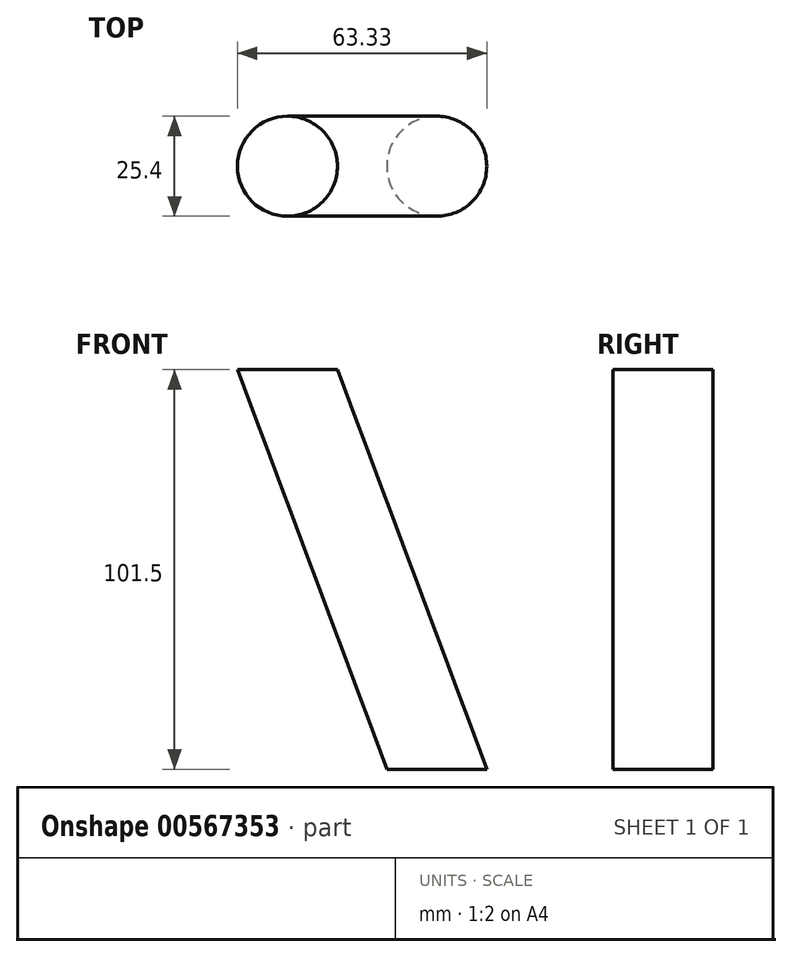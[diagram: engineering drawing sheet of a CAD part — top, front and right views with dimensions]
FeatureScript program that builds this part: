
annotation { "Feature Type Name" : "Feature", "Feature Type Description" : "" }
export const myFeature = defineFeature(function(context is Context, id is Id, definition is map)
    precondition{}
    {
        {
            var Q0;
            Q0=qCreatedBy(makeId("Front.planeOp"),FACE);
            var sketch = newSketch(context, id + "F0", { "sketchPlane" : qUnion([Q0])});
            skLineSegment(sketch, "E0", {"start": v(0, 0) * mm, "end": v(0, 74.43) * mm, "construction": true});
            skLineSegment(sketch, "E1", {"start": v(0, 0) * mm, "end": v(204.24, 0) * mm, "construction": true});
            skLineSegment(sketch, "E2.0", {"start": v(38.1, 0) * mm, "end": v(38.1, 74.43) * mm});
            skLineSegment(sketch, "E3.0", {"start": v(76.2, 0) * mm, "end": v(76.2, 74.43) * mm});
            skSolve(sketch);
        }
        {
            var Q0;
            Q0=qCreatedBy(makeId("Front.planeOp"),FACE);
            var sketch = newSketch(context, id + "F1", { "sketchPlane" : qUnion([Q0])});
            skLineSegment(sketch, "E4", {"start": v(75.9, 0) * mm, "end": v(37.98, 101.5) * mm});
            skSolve(sketch);
        }
        {
            var Q0;
            Q0=qCreatedBy(makeId("Top.planeOp"),FACE);
            var sketch = newSketch(context, id + "F2", { "sketchPlane" : qUnion([Q0])});
            skCircle(sketch, "E5", {"center": v(38.27, 0) * mm, "radius": 12.7 * mm});
            skSolve(sketch);
        }
        {
            var Q0;
            Q0=makeQuery(id+"F2.imprint","IMPRINT",FACE,{"disambiguationData":[TD([[makeQuery(id+"F2.imprint","IMPRINT",EDGE,{"derivedFrom":sQuery(id+"F2.wireOp",EDGE,"E5")}),1.0]])]});
            var Q1;
            Q1=sQuery(id+"F1.wireOp",EDGE,"E4");
            sweep(context, id + "F3", {"profiles" : qUnion([Q0]), "path" : qUnion([Q1])});
        }
    });
